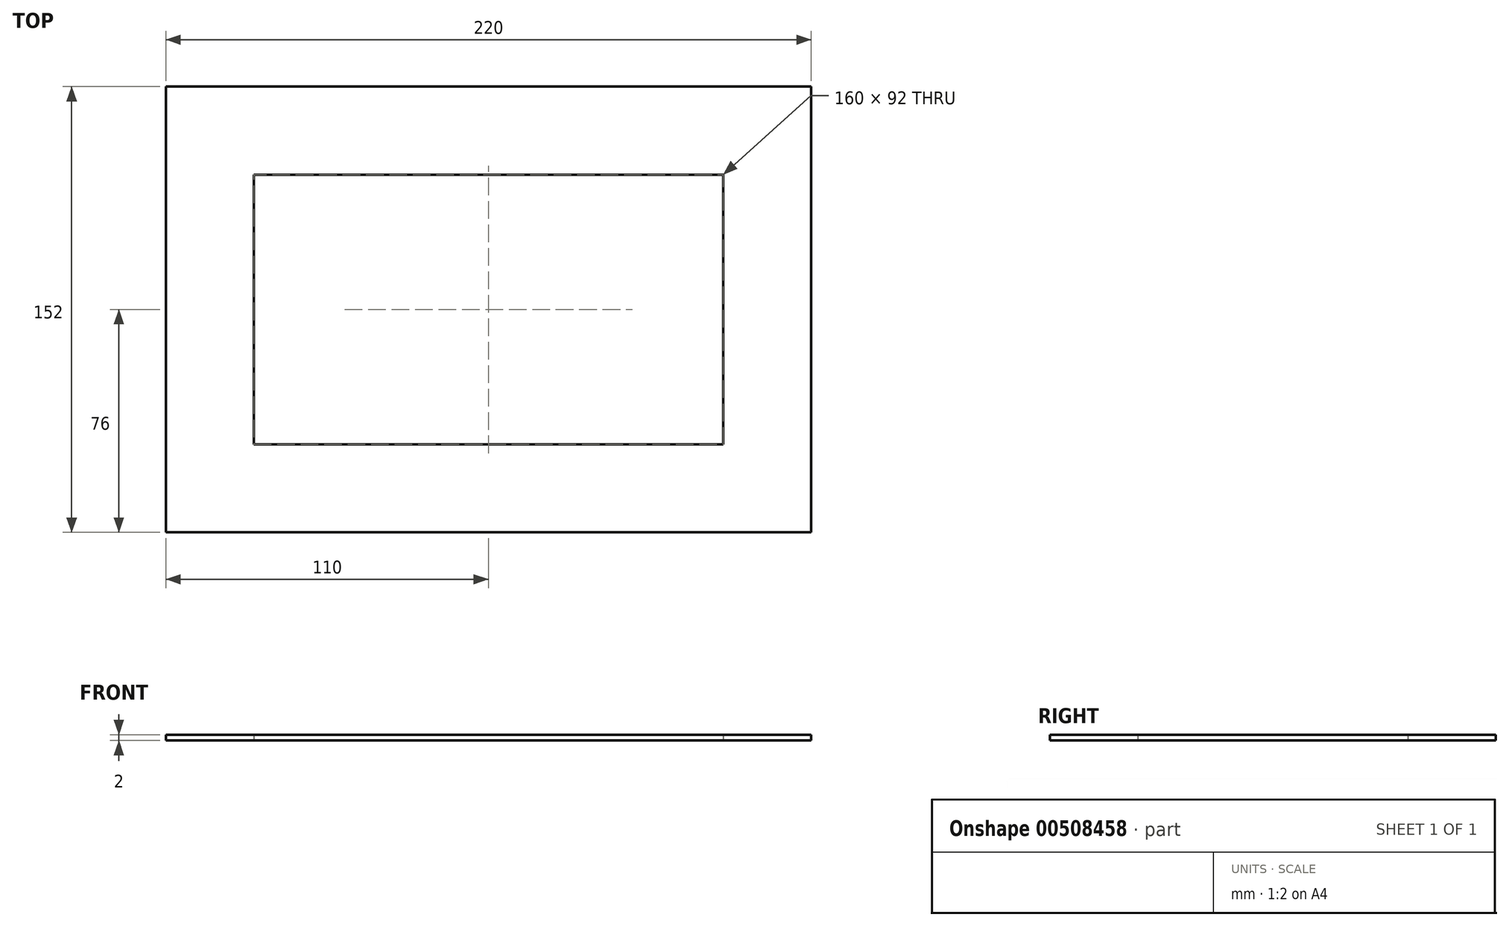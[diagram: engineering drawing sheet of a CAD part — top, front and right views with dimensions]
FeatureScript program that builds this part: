
annotation { "Feature Type Name" : "Feature", "Feature Type Description" : "" }
export const myFeature = defineFeature(function(context is Context, id is Id, definition is map)
    precondition{}
    {
        {
            var Q0;
            Q0=qCreatedBy(makeId("Top.planeOp"),FACE);
            var sketch = newSketch(context, id + "F0", { "sketchPlane" : qUnion([Q0])});
            skLineSegment(sketch, "E0.bottom", {"start": v(-80, 46) * mm, "end": v(80, 46) * mm});
            skLineSegment(sketch, "E0.top", {"start": v(-80, -46) * mm, "end": v(80, -46) * mm});
            skLineSegment(sketch, "E0.left", {"start": v(-80, 46) * mm, "end": v(-80, -46) * mm});
            skLineSegment(sketch, "E0.right", {"start": v(80, 46) * mm, "end": v(80, -46) * mm});
            skLineSegment(sketch, "E1.bottom", {"start": v(-110, 76) * mm, "end": v(110, 76) * mm});
            skLineSegment(sketch, "E1.top", {"start": v(-110, -76) * mm, "end": v(110, -76) * mm});
            skLineSegment(sketch, "E1.left", {"start": v(-110, 76) * mm, "end": v(-110, -76) * mm});
            skLineSegment(sketch, "E1.right", {"start": v(110, 76) * mm, "end": v(110, -76) * mm});
            skSolve(sketch);
        }
        {
            var Q0;
            Q0=makeQuery(id+"F0.imprint","IMPRINT",FACE,{"disambiguationData":[TD([[makeQuery(id+"F0.imprint","IMPRINT",EDGE,{"derivedFrom":sQuery(id+"F0.wireOp",EDGE,"E0.bottom")}),1.0]])]});
            extrude(context, id + "F1", {"entities" : qUnion([Q0]), "depth" : 2 * mm});
        }
    });
